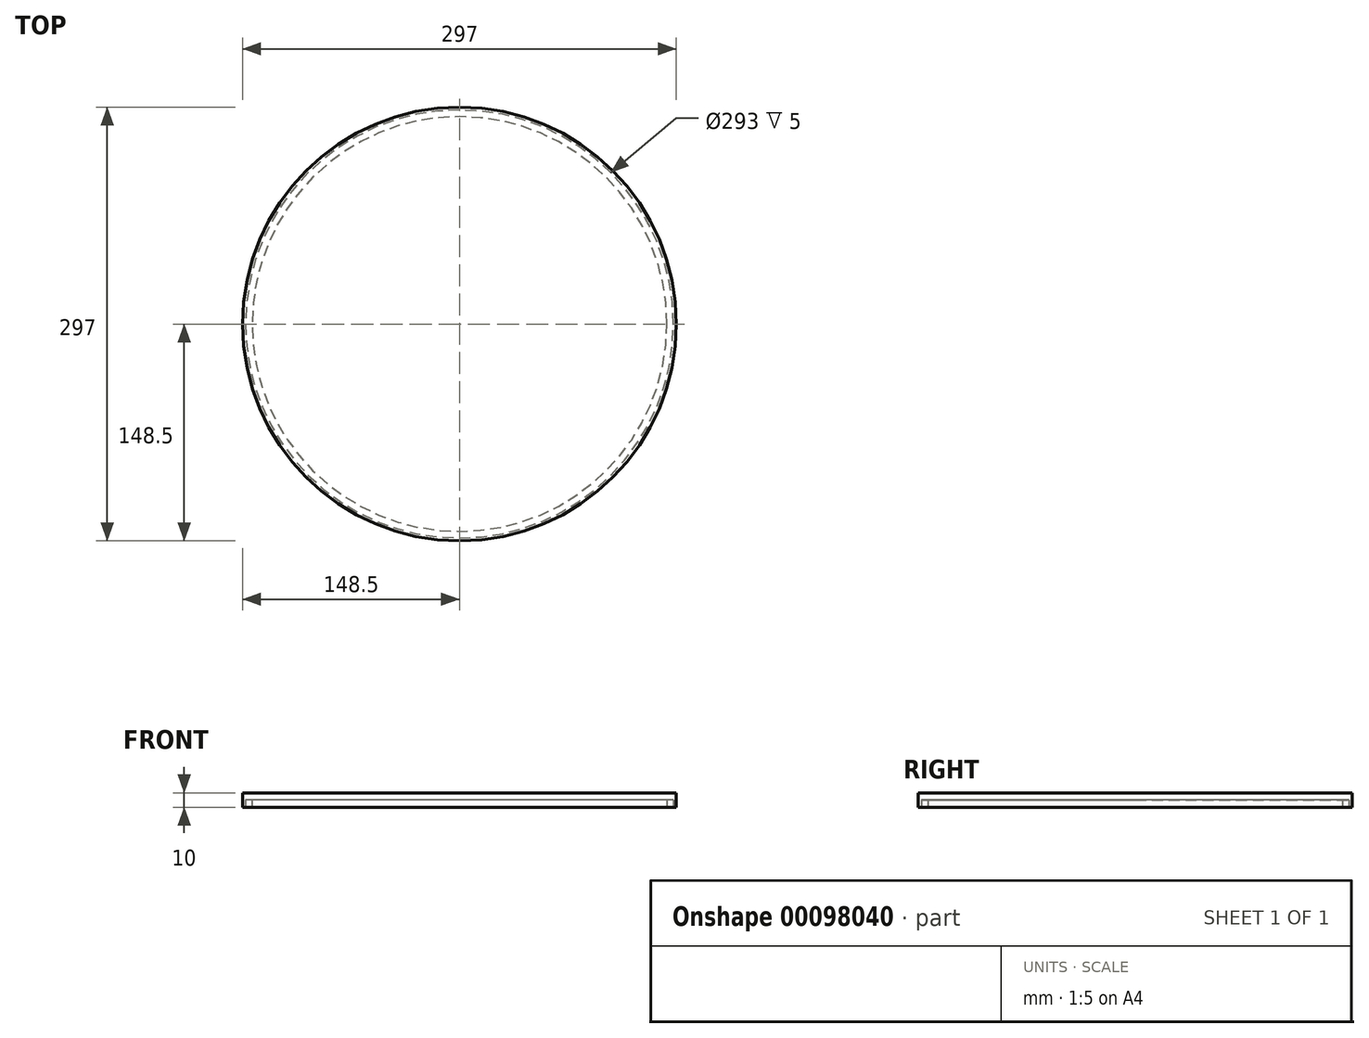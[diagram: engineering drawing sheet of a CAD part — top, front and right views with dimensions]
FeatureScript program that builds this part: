
annotation { "Feature Type Name" : "Feature", "Feature Type Description" : "" }
export const myFeature = defineFeature(function(context is Context, id is Id, definition is map)
    precondition{}
    {
        {
            var Q0;
            Q0=qCreatedBy(makeId("Top.planeOp"),FACE);
            var sketch = newSketch(context, id + "F0", { "sketchPlane" : qUnion([Q0])});
            skCircle(sketch, "E0", {"center": v(0, 0) * mm, "radius": 148.5 * mm});
            skSolve(sketch);
        }
        {
            var Q0;
            Q0=makeQuery(id+"F0.imprint","IMPRINT",FACE,{"disambiguationData":[TD([[makeQuery(id+"F0.imprint","IMPRINT",EDGE,{"derivedFrom":sQuery(id+"F0.wireOp",EDGE,"E0")}),1.0]])]});
            var Q1;
            Q1=makeQuery(id+"F0.imprint","IMPRINT",FACE,{"disambiguationData":[TD([[makeQuery(id+"F0.imprint","IMPRINT",EDGE,{"derivedFrom":sQuery(id+"F0.wireOp",EDGE,"LIXrByum-44Gz-KbWN-PE50-DMeDG7NppI0J")}),1.0]])]});
            var Q2;
            Q2=makeQuery(id+"F0.imprint","IMPRINT",FACE,{"disambiguationData":[TD([[makeQuery(id+"F0.imprint","IMPRINT",EDGE,{"derivedFrom":sQuery(id+"F0.wireOp",EDGE,"oq2Y4278-V4UZ-WgQw-2GIa-DsGsglEtdsp5")}),1.0]])]});
            extrude(context, id + "F1", {"entities" : qUnion([Q0, Q1, Q2]), "depth" : 10 * mm});
        }
        {
            var Q0;
            Q0=makeQuery(id+"F0.imprint","IMPRINT",FACE,{"disambiguationData":[TD([[makeQuery(id+"F0.imprint","IMPRINT",EDGE,{"derivedFrom":sQuery(id+"F0.wireOp",EDGE,"E0")}),1.0]])]});
            var sketch = newSketch(context, id + "F2", { "sketchPlane" : qUnion([Q0])});
            skCircle(sketch, "E1", {"center": v(0, 0) * mm, "radius": 146.5 * mm});
            skCircle(sketch, "E2", {"center": v(0, 0) * mm, "radius": 142 * mm});
            skSolve(sketch);
        }
        {
            var Q0;
            Q0 = qSketchRegion(id + "F2", true);
            extrude(context, id + "F3", {"entities" : qUnion([Q0]), "operationType" : NewBodyOperationType.REMOVE, "depth" : 5 * mm});
        }
    });
